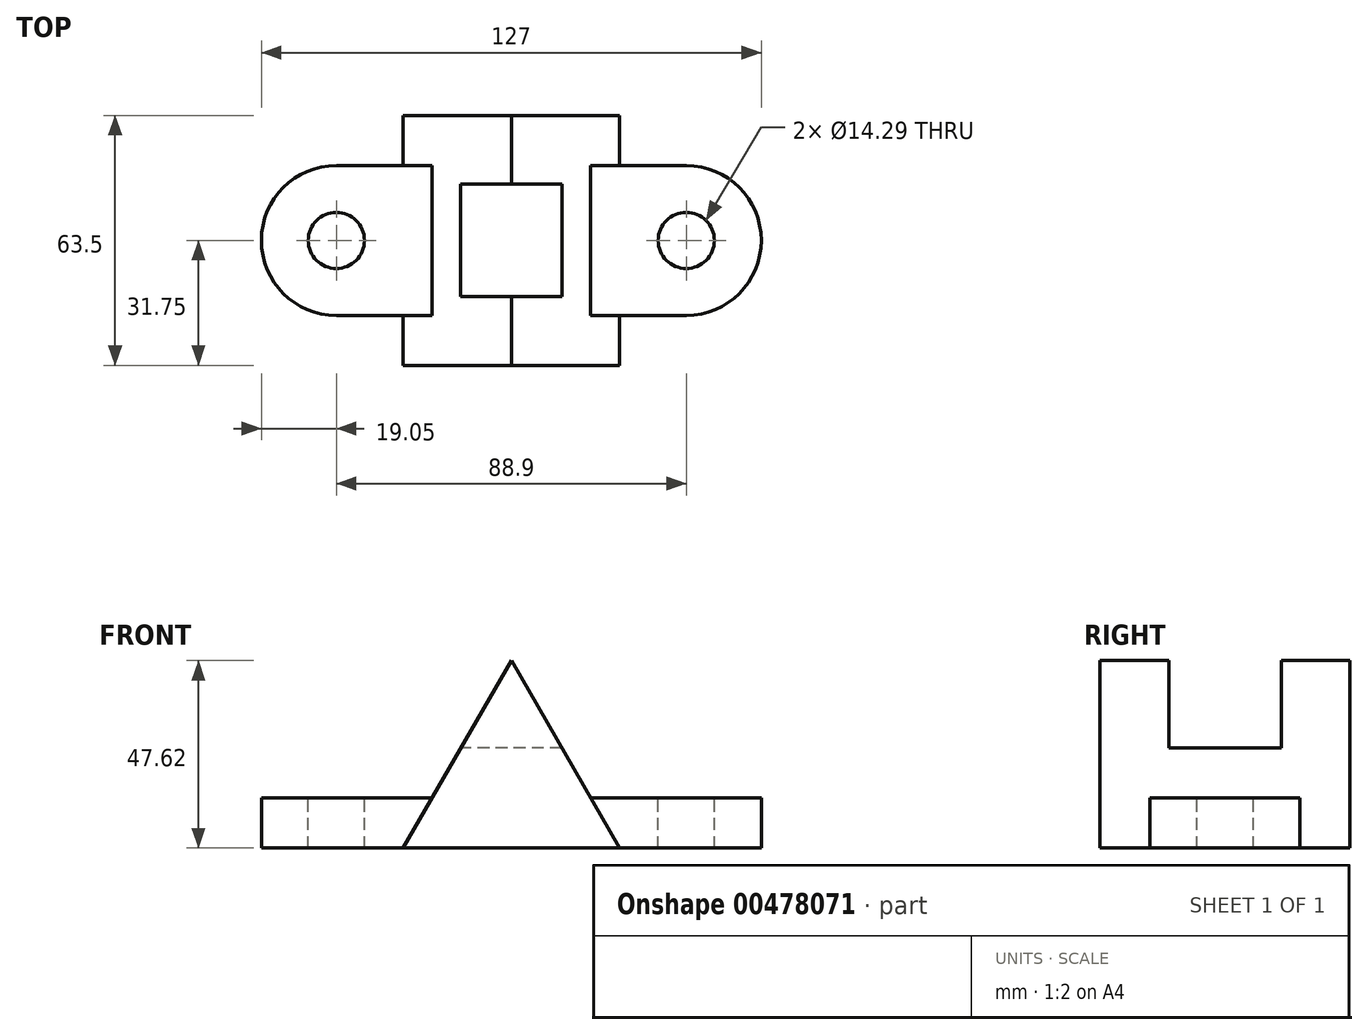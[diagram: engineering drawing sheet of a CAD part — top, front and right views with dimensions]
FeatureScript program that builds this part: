
annotation { "Feature Type Name" : "Feature", "Feature Type Description" : "" }
export const myFeature = defineFeature(function(context is Context, id is Id, definition is map)
    precondition{}
    {
        {
            var Q0;
            Q0=qCreatedBy(makeId("Front.planeOp"),FACE);
            var sketch = newSketch(context, id + "F0", { "sketchPlane" : qUnion([Q0])});
            skLineSegment(sketch, "E0", {"start": v(0, 0) * mm, "end": v(0, 47.63) * mm});
            skLineSegment(sketch, "E1", {"start": v(0, 47.62) * mm, "end": v(-27.5, 0) * mm});
            skLineSegment(sketch, "E2", {"start": v(0, 47.62) * mm, "end": v(27.5, 0) * mm});
            skLineSegment(sketch, "E3", {"start": v(-27.5, 0) * mm, "end": v(27.5, 0) * mm});
            skLineSegment(sketch, "E4", {"start": v(0, 0) * mm, "end": v(-44.45, 0) * mm});
            skLineSegment(sketch, "E5", {"start": v(0, 0) * mm, "end": v(44.45, 0) * mm});
            skLineSegment(sketch, "E6", {"start": v(44.45, 0) * mm, "end": v(44.45, 12.7) * mm});
            skLineSegment(sketch, "E7", {"start": v(44.45, 12.7) * mm, "end": v(-44.45, 12.7) * mm});
            skLineSegment(sketch, "E8", {"start": v(-44.45, 12.7) * mm, "end": v(-44.45, 0) * mm});
            skSolve(sketch);
        }
        {
            var Q0;
            {var subQ0=sQuery(id+"F0.wireOp",EDGE,"E2");var subQ3=sQuery(id+"F0.wireOp",EDGE,"E7");var subQ5=makeQuery(id+"F0.imprint","INTERSECT",VERTEX,{"derivedFrom":[subQ0,subQ3]});Q0=makeQuery(id+"F0.imprint","IMPRINT",FACE,{"disambiguationData":[TD([[makeQuery(id+"F0.imprint","IMPRINT",EDGE,{"disambiguationData":[TD([[subQ5,-1.0]])],"derivedFrom":subQ3}),-1.0]])]});}
            var Q1;
            {var subQ0=sQuery(id+"F0.wireOp",EDGE,"E4");var subQ5=sQuery(id+"F0.wireOp",EDGE,"E1");var subQ6=makeQuery(id+"F0.imprint","INTERSECT",VERTEX,{"derivedFrom":[subQ5,subQ0]});Q1=makeQuery(id+"F0.imprint","IMPRINT",FACE,{"disambiguationData":[TD([[makeQuery(id+"F0.imprint","IMPRINT",EDGE,{"disambiguationData":[TD([[subQ6,1.0]])],"derivedFrom":subQ5}),1.0]])]});}
            var Q2;
            {var subQ0=sQuery(id+"F0.wireOp",EDGE,"E5");var subQ5=sQuery(id+"F0.wireOp",EDGE,"E2");var subQ6=makeQuery(id+"F0.imprint","INTERSECT",VERTEX,{"derivedFrom":[subQ5,subQ0]});Q2=makeQuery(id+"F0.imprint","IMPRINT",FACE,{"disambiguationData":[TD([[makeQuery(id+"F0.imprint","IMPRINT",EDGE,{"disambiguationData":[TD([[subQ6,1.0]])],"derivedFrom":subQ5}),-1.0]])]});}
            var Q3;
            {var subQ0=sQuery(id+"F0.wireOp",EDGE,"E1");var subQ3=sQuery(id+"F0.wireOp",EDGE,"E7");var subQ5=makeQuery(id+"F0.imprint","INTERSECT",VERTEX,{"derivedFrom":[subQ0,subQ3]});Q3=makeQuery(id+"F0.imprint","IMPRINT",FACE,{"disambiguationData":[TD([[makeQuery(id+"F0.imprint","IMPRINT",EDGE,{"disambiguationData":[TD([[subQ5,1.0]])],"derivedFrom":subQ3}),-1.0]])]});}
            extrude(context, id + "F1", {"entities" : qUnion([Q0, Q1, Q2, Q3]), "endBound" : BoundingType.SYMMETRIC, "depth" : 63.5 * mm});
        }
        {
            var Q0;
            Q0 = qSketchRegion(id + "F0", true);
            extrude(context, id + "F2", {"entities" : qUnion([Q0]), "operationType" : NewBodyOperationType.ADD, "endBound" : BoundingType.SYMMETRIC, "depth" : 38.1 * mm});
        }
        {
            var Q0;
            {var subQ0=sQuery(id+"F0.wireOp",EDGE,"E7");Q0=makeQuery(id+"F2.opExtrude","SWEPT_FACE",FACE,{"disambiguationData":[OSD([subQ0]),TDD([makeQuery(id+"F0.imprint","IMPRINT",EDGE,{"disambiguationData":[TD([[makeQuery(id+"F0.imprint","INTERSECT",VERTEX,{"derivedFrom":[subQ0,sQuery(id+"F0.wireOp",EDGE,"E8")]}),1.0]])],"derivedFrom":subQ0})])]});}
            var sketch = newSketch(context, id + "F3", { "sketchPlane" : qUnion([Q0])});
            skCircle(sketch, "E9", {"center": v(-44.45, 0) * mm, "radius": 19.05 * mm});
            skCircle(sketch, "E10", {"center": v(-44.45, 0) * mm, "radius": 7.14 * mm});
            skSolve(sketch);
        }
        {
            var Q0;
            {var subQ0=sQuery(id+"F0.wireOp",EDGE,"E7");Q0=makeQuery(id+"F2.opExtrude","SWEPT_FACE",FACE,{"disambiguationData":[OSD([subQ0]),TDD([makeQuery(id+"F0.imprint","IMPRINT",EDGE,{"disambiguationData":[TD([[makeQuery(id+"F0.imprint","INTERSECT",VERTEX,{"derivedFrom":[sQuery(id+"F0.wireOp",EDGE,"E6"),subQ0]}),-1.0]])],"derivedFrom":subQ0})])]});}
            var sketch = newSketch(context, id + "F4", { "sketchPlane" : qUnion([Q0])});
            skCircle(sketch, "E11", {"center": v(44.45, 0) * mm, "radius": 19.05 * mm});
            skCircle(sketch, "E12", {"center": v(44.45, 0) * mm, "radius": 7.14 * mm});
            skSolve(sketch);
        }
        {
            var Q0;
            Q0 = qSketchRegion(id + "F4", true);
            var Q1;
            {var subQ1=sQuery(id+"F0.wireOp",EDGE,"E8");var subQ2=sQuery(id+"F0.wireOp",EDGE,"E7");var subQ4=makeQuery(id+"F2.opExtrude","SWEPT_EDGE",EDGE,{"disambiguationData":[OSD([subQ2,subQ1])]});Q1=makeQuery(id+"F3.imprint","IMPRINT",FACE,{"disambiguationData":[TD([[makeQuery(id+"F3.imprint","IMPRINT",EDGE,{"derivedFrom":subQ4}),1.0]])]});}
            var Q2;
            {var subQ0=sQuery(id+"F0.wireOp",EDGE,"E5");var subQ1=sQuery(id+"F0.wireOp",EDGE,"E4");Q2=makeQuery(id+"F2.boolean.opBoolean","MERGE",FACE,{"derivedFrom":[makeQuery(id+"F1.opExtrude","SWEPT_FACE",FACE,{"disambiguationData":[OSD([subQ1,subQ0])]}),makeQuery(id+"F2.opExtrude","SWEPT_FACE",FACE,{"disambiguationData":[OSD([subQ1,subQ0])]})]});}
            extrude(context, id + "F5", {"entities" : qUnion([Q0, Q1]), "operationType" : NewBodyOperationType.ADD, "endBound" : BoundingType.UP_TO_SURFACE, "oppositeDirection" : true, "endBoundEntityFace" : qUnion([Q2]), "depth" : 25.4 * mm});
        }
        {
            var Q0;
            {var subQ0=sQuery(id+"F3.wireOp",EDGE,"E10");var subQ1=makeQuery(id+"F2.opExtrude","SWEPT_EDGE",EDGE,{"disambiguationData":[OSD([sQuery(id+"F0.wireOp",EDGE,"E7"),sQuery(id+"F0.wireOp",EDGE,"E8")])]});var subQ2=makeQuery(id+"F3.imprint","INTERSECT",VERTEX,{"disambiguationData":[OD(0.0)],"derivedFrom":[subQ1,subQ0]});Q0=makeQuery(id+"F3.imprint","IMPRINT",FACE,{"disambiguationData":[TD([[makeQuery(id+"F3.imprint","IMPRINT",EDGE,{"disambiguationData":[TD([[subQ2,1.0]])],"derivedFrom":subQ0}),1.0]])]});}
            var Q1;
            {var subQ0=sQuery(id+"F3.wireOp",EDGE,"E10");var subQ1=makeQuery(id+"F2.opExtrude","SWEPT_EDGE",EDGE,{"disambiguationData":[OSD([sQuery(id+"F0.wireOp",EDGE,"E7"),sQuery(id+"F0.wireOp",EDGE,"E8")])]});var subQ2=makeQuery(id+"F3.imprint","INTERSECT",VERTEX,{"disambiguationData":[OD(0.0)],"derivedFrom":[subQ1,subQ0]});Q1=makeQuery(id+"F3.imprint","IMPRINT",FACE,{"disambiguationData":[TD([[makeQuery(id+"F3.imprint","IMPRINT",EDGE,{"disambiguationData":[TD([[subQ2,-1.0]])],"derivedFrom":subQ0}),1.0]])]});}
            extrude(context, id + "F6", {"entities" : qUnion([Q0, Q1]), "operationType" : NewBodyOperationType.REMOVE, "oppositeDirection" : true, "depth" : 25.4 * mm});
        }
        {
            var Q0;
            {var subQ0=sQuery(id+"F4.wireOp",EDGE,"E12");var subQ1=makeQuery(id+"F2.opExtrude","SWEPT_EDGE",EDGE,{"disambiguationData":[OSD([sQuery(id+"F0.wireOp",EDGE,"E6"),sQuery(id+"F0.wireOp",EDGE,"E7")])]});var subQ2=makeQuery(id+"F4.imprint","INTERSECT",VERTEX,{"disambiguationData":[OD(0.0)],"derivedFrom":[subQ1,subQ0]});Q0=makeQuery(id+"F4.imprint","IMPRINT",FACE,{"disambiguationData":[TD([[makeQuery(id+"F4.imprint","IMPRINT",EDGE,{"disambiguationData":[TD([[subQ2,-1.0]])],"derivedFrom":subQ0}),1.0]])]});}
            extrude(context, id + "F7", {"entities" : qUnion([Q0]), "operationType" : NewBodyOperationType.REMOVE, "oppositeDirection" : true, "depth" : 25.4 * mm});
        }
        {
            var Q0;
            Q0=qCreatedBy(makeId("Front.planeOp"),FACE);
            var sketch = newSketch(context, id + "F8", { "sketchPlane" : qUnion([Q0])});
            skLineSegment(sketch, "E13", {"start": v(0, 0) * mm, "end": v(0, 47.63) * mm});
            skLineSegment(sketch, "E14", {"start": v(0, 47.63) * mm, "end": v(0, 25.4) * mm});
            skLineSegment(sketch, "E15", {"start": v(0, 25.4) * mm, "end": v(-40.19, 25.4) * mm});
            skLineSegment(sketch, "E16", {"start": v(-40.19, 25.4) * mm, "end": v(-40.19, 47.63) * mm});
            skLineSegment(sketch, "E17", {"start": v(-40.19, 47.63) * mm, "end": v(32.26, 47.63) * mm});
            skLineSegment(sketch, "E18", {"start": v(32.26, 47.63) * mm, "end": v(32.26, 25.4) * mm});
            skLineSegment(sketch, "E19", {"start": v(32.26, 25.4) * mm, "end": v(0, 25.4) * mm});
            skSolve(sketch);
        }
        {
            var Q0;
            Q0 = qSketchRegion(id + "F8", true);
            extrude(context, id + "F9", {"entities" : qUnion([Q0]), "operationType" : NewBodyOperationType.REMOVE, "endBound" : BoundingType.SYMMETRIC, "oppositeDirection" : true, "depth" : 28.57 * mm});
        }
    });
